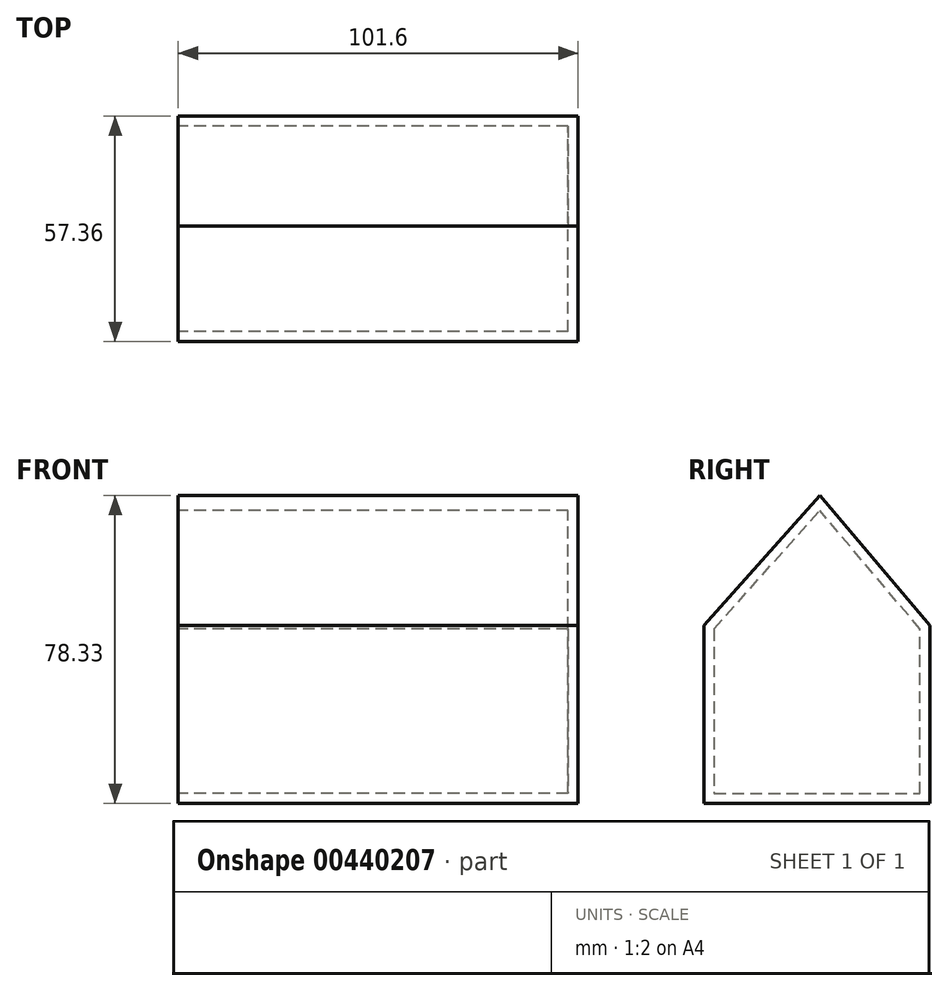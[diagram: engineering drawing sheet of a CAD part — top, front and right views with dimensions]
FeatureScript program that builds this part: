
annotation { "Feature Type Name" : "Feature", "Feature Type Description" : "" }
export const myFeature = defineFeature(function(context is Context, id is Id, definition is map)
    precondition{}
    {
        {
            var Q0;
            Q0=qCreatedBy(makeId("Right.planeOp"),FACE);
            var sketch = newSketch(context, id + "F0", { "sketchPlane" : qUnion([Q0])});
            skLineSegment(sketch, "E0", {"start": v(-29.4, 16.87) * mm, "end": v(-29.4, -28.44) * mm});
            skLineSegment(sketch, "E1", {"start": v(-29.4, -28.44) * mm, "end": v(27.96, -28.44) * mm});
            skLineSegment(sketch, "E2", {"start": v(27.96, -28.44) * mm, "end": v(27.96, 16.87) * mm});
            skLineSegment(sketch, "E3", {"start": v(27.96, 16.87) * mm, "end": v(-29.4, 16.87) * mm});
            skLineSegment(sketch, "E4", {"start": v(-29.4, 16.87) * mm, "end": v(0, 49.89) * mm});
            skLineSegment(sketch, "E5", {"start": v(27.96, 16.87) * mm, "end": v(0, 49.89) * mm});
            skLineSegment(sketch, "E6", {"start": v(0, 49.89) * mm, "end": v(0, 49.89) * mm});
            skSolve(sketch);
        }
        {
            var Q0;
            Q0 = qSketchRegion(id + "F0", true);
            extrude(context, id + "F1", {"entities" : qUnion([Q0]), "depth" : 101.6 * mm});
        }
        {
            var Q0;
            Q0=makeQuery(id+"F1.opExtrude","CAP_FACE",FACE,{"disambiguationData":[OSD([sQuery(id+"F0.wireOp",EDGE,"E0"),sQuery(id+"F0.wireOp",EDGE,"E1"),sQuery(id+"F0.wireOp",EDGE,"E2"),sQuery(id+"F0.wireOp",EDGE,"E4"),sQuery(id+"F0.wireOp",EDGE,"E5")])],"isStart":true});
            shell(context, id + "F2", {"entities" : qUnion([Q0]), "thickness" : 2.54 * mm});
        }
    });
